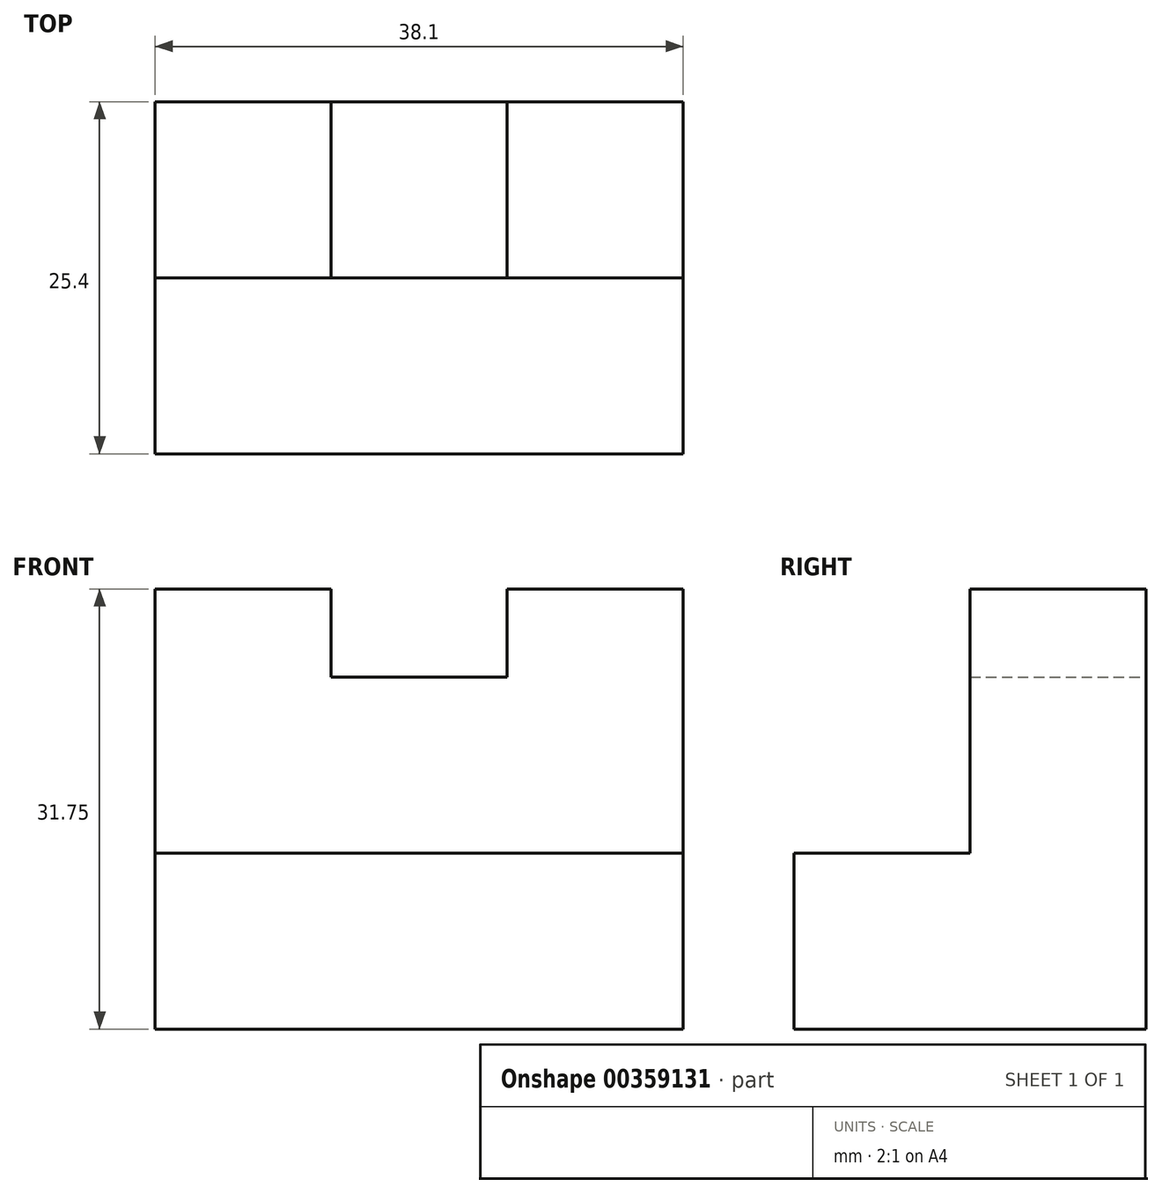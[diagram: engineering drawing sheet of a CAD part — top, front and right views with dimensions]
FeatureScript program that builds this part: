
annotation { "Feature Type Name" : "Feature", "Feature Type Description" : "" }
export const myFeature = defineFeature(function(context is Context, id is Id, definition is map)
    precondition{}
    {
        {
            var Q0;
            Q0=qCreatedBy(makeId("Front.planeOp"),FACE);
            var sketch = newSketch(context, id + "F0", { "sketchPlane" : qUnion([Q0])});
            skLineSegment(sketch, "E0", {"start": v(-43.16, 36.46) * mm, "end": v(-43.16, 4.7) * mm});
            skLineSegment(sketch, "E1", {"start": v(-43.16, 4.7) * mm, "end": v(-5.06, 4.7) * mm});
            skLineSegment(sketch, "E2", {"start": v(-5.06, 4.7) * mm, "end": v(-5.06, 36.46) * mm});
            skLineSegment(sketch, "E3", {"start": v(-5.06, 36.46) * mm, "end": v(-17.76, 36.46) * mm});
            skLineSegment(sketch, "E4", {"start": v(-17.76, 36.46) * mm, "end": v(-17.76, 30.1) * mm});
            skLineSegment(sketch, "E5", {"start": v(-17.76, 30.1) * mm, "end": v(-30.46, 30.1) * mm});
            skLineSegment(sketch, "E6", {"start": v(-30.46, 30.1) * mm, "end": v(-30.46, 36.46) * mm});
            skLineSegment(sketch, "E7", {"start": v(-43.16, 36.46) * mm, "end": v(-30.46, 36.46) * mm});
            skSolve(sketch);
        }
        {
            var Q0;
            Q0=makeQuery(id+"F0.imprint","IMPRINT",FACE,{"disambiguationData":[TD([[makeQuery(id+"F0.imprint","IMPRINT",EDGE,{"derivedFrom":sQuery(id+"F0.wireOp",EDGE,"E0")}),1.0]])]});
            extrude(context, id + "F1", {"entities" : qUnion([Q0]), "depth" : 25.4 * mm});
        }
        {
            var Q0;
            Q0=makeQuery(id+"F1.opExtrude","CAP_FACE",FACE,{"disambiguationData":[OSD([sQuery(id+"F0.wireOp",EDGE,"E0"),sQuery(id+"F0.wireOp",EDGE,"E1"),sQuery(id+"F0.wireOp",EDGE,"E2"),sQuery(id+"F0.wireOp",EDGE,"E3"),sQuery(id+"F0.wireOp",EDGE,"E4"),sQuery(id+"F0.wireOp",EDGE,"E5"),sQuery(id+"F0.wireOp",EDGE,"E6"),sQuery(id+"F0.wireOp",EDGE,"E7")])],"isStart":false});
            extrude(context, id + "F2", {"entities" : qUnion([Q0]), "operationType" : NewBodyOperationType.ADD, "oppositeDirection" : true, "depth" : 12.7 * mm});
        }
        {
            var Q0;
            Q0=makeQuery(id+"F1.opExtrude","CAP_FACE",FACE,{"disambiguationData":[OSD([sQuery(id+"F0.wireOp",EDGE,"E0"),sQuery(id+"F0.wireOp",EDGE,"E1"),sQuery(id+"F0.wireOp",EDGE,"E2"),sQuery(id+"F0.wireOp",EDGE,"E3"),sQuery(id+"F0.wireOp",EDGE,"E4"),sQuery(id+"F0.wireOp",EDGE,"E5"),sQuery(id+"F0.wireOp",EDGE,"E6"),sQuery(id+"F0.wireOp",EDGE,"E7")])],"isStart":false});
            var sketch = newSketch(context, id + "F3", { "sketchPlane" : qUnion([Q0])});
            skLineSegment(sketch, "E8", {"start": v(-43.16, 17.4) * mm, "end": v(-5.06, 17.4) * mm});
            skSolve(sketch);
        }
        {
            var Q0;
            {var subQ1=sQuery(id+"F3.wireOp",EDGE,"E8");Q0=makeQuery(id+"F3.imprint","IMPRINT",FACE,{"disambiguationData":[TD([[makeQuery(id+"F3.imprint","IMPRINT",EDGE,{"derivedFrom":subQ1}),1.0]])]});}
            extrude(context, id + "F4", {"entities" : qUnion([Q0]), "operationType" : NewBodyOperationType.REMOVE, "oppositeDirection" : true, "depth" : 12.7 * mm});
        }
    });
